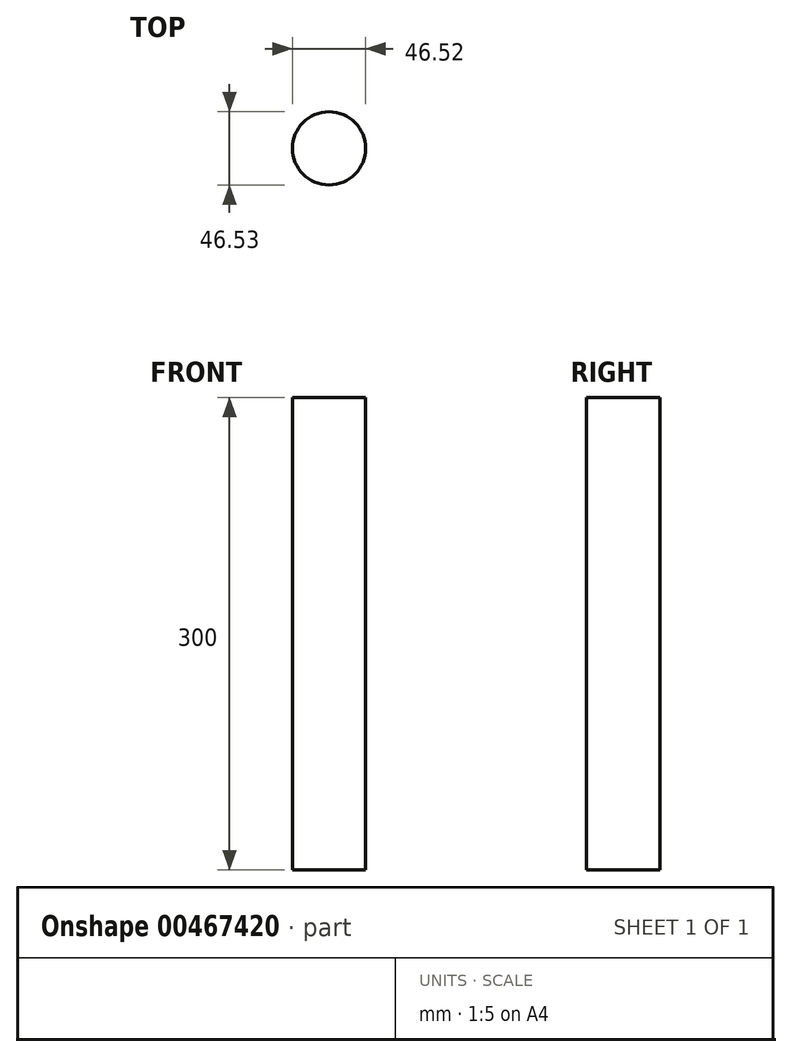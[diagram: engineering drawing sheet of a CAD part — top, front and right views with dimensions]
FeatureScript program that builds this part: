
annotation { "Feature Type Name" : "Feature", "Feature Type Description" : "" }
export const myFeature = defineFeature(function(context is Context, id is Id, definition is map)
    precondition{}
    {
        {
            var Q0;
            Q0=qCreatedBy(makeId("Top.planeOp"),FACE);
            var sketch = newSketch(context, id + "F0", { "sketchPlane" : qUnion([Q0])});
            skCircle(sketch, "E0", {"center": v(-42.19, 26.4) * mm, "radius": 23.26 * mm});
            skSolve(sketch);
        }
        {
            var Q0;
            Q0=makeQuery(id+"F0.imprint","IMPRINT",FACE,{"disambiguationData":[TD([[makeQuery(id+"F0.imprint","IMPRINT",EDGE,{"derivedFrom":sQuery(id+"F0.wireOp",EDGE,"E0")}),1.0]])]});
            extrude(context, id + "F1", {"entities" : qUnion([Q0]), "depth" : 300 * mm});
        }
    });
